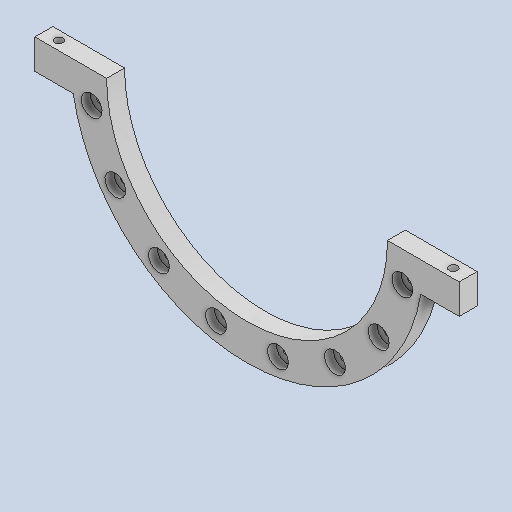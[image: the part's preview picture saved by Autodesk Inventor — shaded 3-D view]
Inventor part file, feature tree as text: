
AUTODESK INVENTOR PART (.ipt)
format: ipt  version: 2025 (Build 290162010, 162A)  size: 239,104 bytes
history: native  units: mm
features: sketch x4, extrude x2, hole x2, mirror x2, other x2, fillet x1, pattern_circular x1
ambient origin geometry x8: Origin, YZ Plane, XZ Plane, XY Plane, X Axis, Y Axis, Z Axis, Center Point
bodies: Solid1 (feature_tree)
feature tree (14):
  extrude  "Extrusion1"  Depth=30.0mm
  sketch  "Sketch4"  dims[d27=265.0mm d35=1.963495mm]
  sketch  "Sketch7"  dims[d36=60.0mm d40=60.0mm d41=50.0mm]
  fillet  "Fillet1"  Radius=80.0mm
  hole  "Hole1"  [1 undecoded]
  hole  "Hole2"  [1 undecoded]
  pattern_circular  "Circular Pattern4"  Count=5  [1 undecoded]
  mirror  "Mirror1"
  extrude  "Extrusion8"  Depth=10.0mm
  mirror  "Mirror2"
  other  "A-Side Definition"
  sketch  "Sketch1"  dims[d2=30.0mm d3=0.0mm d13=530.0mm d26=80.0mm]
  sketch  "Sketch9"  dims[d42=25.0mm d45=10.0mm d46=14.0mm d47=32.0mm d48=24.0mm d49=15.0mm d50=90.0deg d51=8.0mm d52=20.594885mm d53=13.0mm d54=6.0mm d55=35.0mm d56=15.0mm d57=90.0deg d58=8.0mm d59=20.594885mm d60=90.0mm d61=180.0deg d70=25.0mm d71=14.0mm d72=0.0mm d73=0.0mm d63=1.0mm d64=1.0mm d65=1.0mm d66=0.15mm d67=0.25mm d68=0.375mm d69=14.3117mm d74=0.375mm]
  other  "Definition1"
note: 3 required parameter values undecoded (feature->parameter linkage not recoverable at this tier; creation-order binding heuristic only, values carry confidence <= 0.55)
